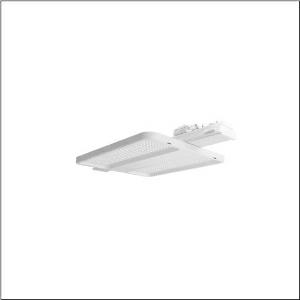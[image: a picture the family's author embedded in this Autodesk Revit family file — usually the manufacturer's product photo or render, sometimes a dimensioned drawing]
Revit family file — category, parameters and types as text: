
# Revit family: highbay_11_fur_licross_tragschiene_midi_51hn11da4mla
name_source: partatom
category: Lighting Fixtures
units: mm (PartAtom-declared; Revit-internal decimal feet)

## family parameters
Cut with Voids When Loaded = No
Host = Face
Light Source = No
Part Type = Normal
Room Calculation Point = No
Round Connector Dimension = Use Diameter
Shared = No

## types (1)
- --- (1 x LED, 28000 lm, 146.6 W, 4000K)
    Apparent Load = 147 VA
    CIE Flux Codes = 85 97 100 100 100
    Color Rendering = 80
    Color Temperature = 4000K
    Default Elevation = 1800 mm
    Description = high bay luminaire Highbay 11 for Licross trunking rail midi; direct symmetric narrow distribution, light control with lens of PMMA; UGR ≤ 22 (X = 4H | Y = 8H | S = 0.25H | reflection values 70/50/20); luminous flux: 28.000lm; light colour: 840, colour temperature: 4000K, MacAdam ≤ 2 SDCM (initial), colour rendering: CRI > 80; luminous efficacy: 191lm/W; rated service life: 100.000h (L95) at AT= 25°C; control: DALI 2; luminaire connection: plug, 5-pole, with phase selectionmains connection: 230..240V, AC 50/60Hz; connected load: 146,6W; protection rating (complete): IP64; insulation class (complete): insulation class I (protective earthing); protection symbol: D; impact resistance: IK06; certification: CE, ENEC, VDE, UKCA; internal wiring halogen-free; luminaire LABS conformity tested according to VDMA 24364:2018-05; Suitable for use in the food industry according to the specifications of IFS-Food, HACCP and/or BRC; housing frame of high-performance plastic PA6, matt traffic white (RAL 9016); cover of PMMA; fixing on rail side of steel, galvanised, white; blank cover of PC/ABS, traffic white (RAL 9016); dimension (LxWxH): 750 x 442 x 71mm; permissible operating ambient temperature: -40..+50°C (reducing of maximum allowable ambient temperature of 5°C with ceiling mounting); packaging unit: 1 piece
    Height = 72 mm  [stored 0.23622 ft]
    Lamp = 1 x LED
    Lamp Light Flux = 28000 lm
    Lamp Power = 146.6 W
    Lamp count = 1
    Length = 474 mm
    Luminous efficacy = 191 lm/W
    Manufacturer = Siteco
    ModVariant = No
    Model = 51HN11DA4MLA
    Mounting Place = Ceiling
    Mounting Type = Pendant
    Number of Poles = 1
    OnlyDefault = Yes
    Power Factor = 1
    Product Name = Highbay 11 für Licross Tragschiene midi
    Product group = high bay luminaire
    ProductGroupID = 902
    Protection Class = Protection class I
    Protection Degree = IP 64
    RLX_Detail_Level = 1
    RLX_Emergency_Light_Flux = 0 lm
    RLX_Emergency_Type = 0
    RLX_Emergency_Type_DB = No
    RlxData = <blob elided: 17153 chars, md5=68a39d5e>
    Socket = socket
    Standby Power = 0 W
    System Light Flux = 28001 lm
    System Power = 147 W
    Type Comments = factory setting: luminous flux: 100 % | dim-lin: 254 | 661 mA
    Type Image = l_1363258.jpg
    URL = http://relux.com
    VarID = @adj_024453
    Voltage = 0 V
    Weight = 0.00 kg
    Width = 442 mm

note: [stored X ft] marks values corroborated as IEEE doubles in the binary element streams (Revit-internal decimal feet)

## geometry (parser evidence)
native form markers: Blend x4, Sweep x12
no freeform markers — native parametric forms only
